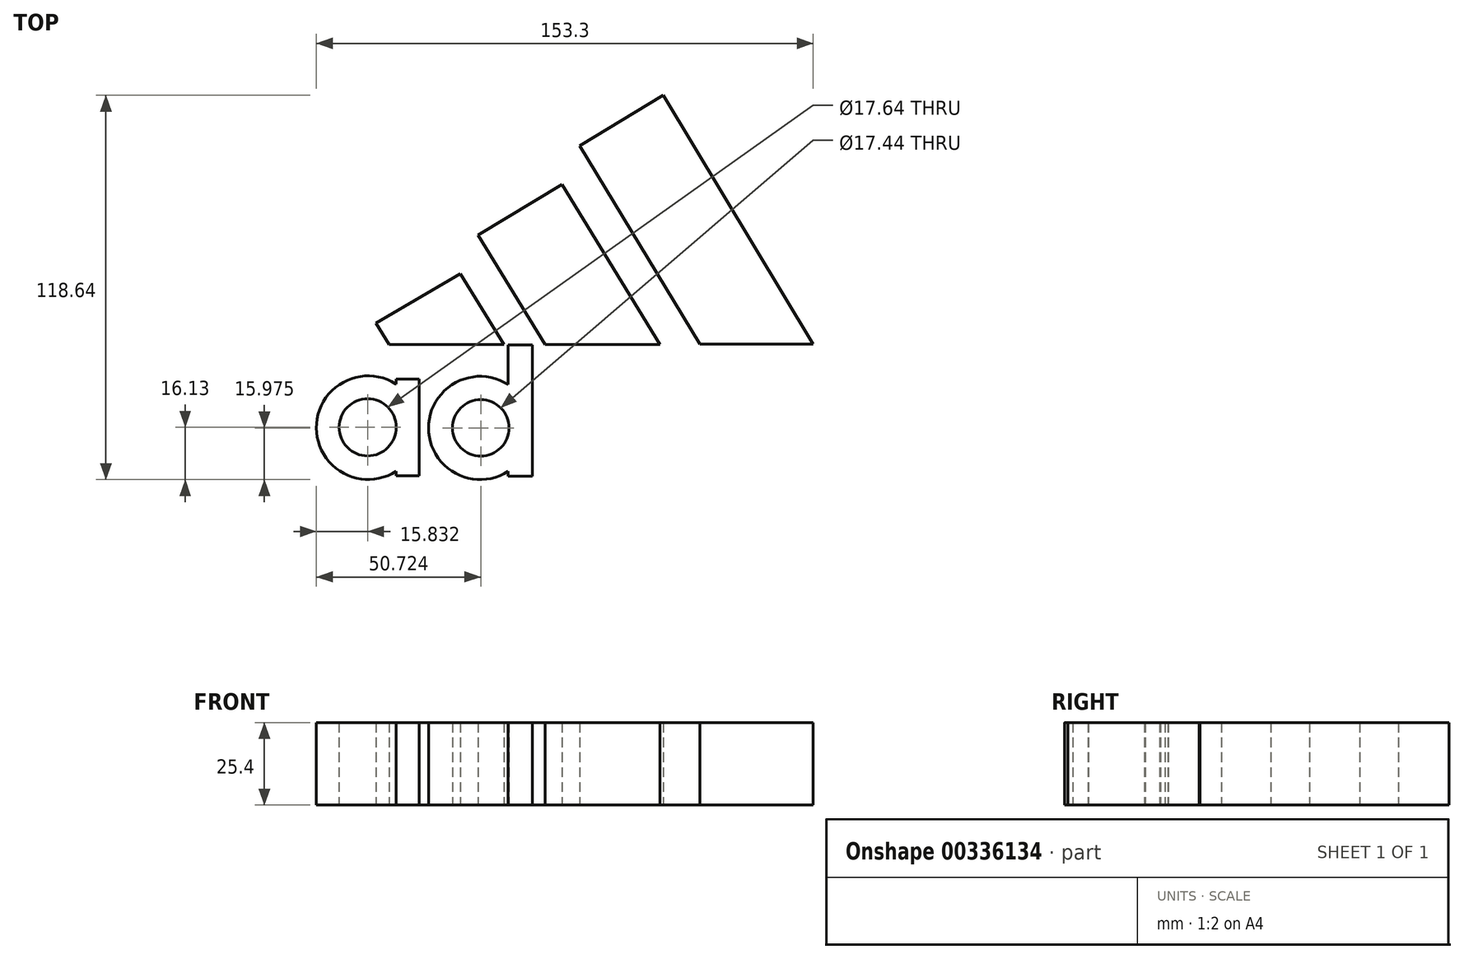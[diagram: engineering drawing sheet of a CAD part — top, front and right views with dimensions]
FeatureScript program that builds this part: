
annotation { "Feature Type Name" : "Feature", "Feature Type Description" : "" }
export const myFeature = defineFeature(function(context is Context, id is Id, definition is map)
    precondition{}
    {
        {
            var Q0;
            Q0=qCreatedBy(makeId("Top.planeOp"),FACE);
            var sketch = newSketch(context, id + "F0", { "sketchPlane" : qUnion([Q0])});
            skLineSegment(sketch, "E0", {"start": v(-45.16, 1.7) * mm, "end": v(-31.76, -20.22) * mm});
            skLineSegment(sketch, "E1", {"start": v(-31.76, -20.22) * mm, "end": v(-67.13, -20.22) * mm});
            skLineSegment(sketch, "E2", {"start": v(-67.13, -20.22) * mm, "end": v(-71.16, -13.54) * mm});
            skLineSegment(sketch, "E3", {"start": v(-71.16, -13.54) * mm, "end": v(-45.16, 1.7) * mm});
            skLineSegment(sketch, "E4", {"start": v(-13.78, 29.19) * mm, "end": v(16.4, -20.22) * mm});
            skLineSegment(sketch, "E5", {"start": v(16.4, -20.22) * mm, "end": v(-19, -20.22) * mm});
            skLineSegment(sketch, "E6", {"start": v(-19, -20.22) * mm, "end": v(-39.69, 13.63) * mm});
            skLineSegment(sketch, "E7", {"start": v(-39.69, 13.63) * mm, "end": v(-13.78, 29.19) * mm});
            skLineSegment(sketch, "E8", {"start": v(17.46, 56.75) * mm, "end": v(63.72, -20.11) * mm});
            skLineSegment(sketch, "E9", {"start": v(63.72, -20.11) * mm, "end": v(28.79, -20.11) * mm});
            skLineSegment(sketch, "E10", {"start": v(28.79, -20.11) * mm, "end": v(-8.37, 41.15) * mm});
            skLineSegment(sketch, "E11", {"start": v(-8.37, 41.15) * mm, "end": v(17.46, 56.75) * mm});
            skCircle(sketch, "E12", {"center": v(-73.75, -45.76) * mm, "radius": 8.82 * mm});
            skPoint(sketch, "E12.first.point", {"position": v(-73.75, -36.94) * mm});
            skPoint(sketch, "E12.second.point", {"position": v(-64.93, -45.5) * mm});
            skPoint(sketch, "E12.third.point", {"position": v(-80.69, -51.2) * mm});
            skArc(sketch, "E13", {"start": v(-65.08, -32.32) * mm, "mid": v(-89.58, -45.94) * mm, "end": v(-64.93, -59.3) * mm});
            skArc(sketch, "E14", {"start": v(-30.4, -32.55) * mm, "mid": v(-54.97, -45.93) * mm, "end": v(-30.43, -59.37) * mm});
            skCircle(sketch, "E15", {"center": v(-38.86, -45.92) * mm, "radius": 8.72 * mm});
            skPoint(sketch, "E15.first.point", {"position": v(-47.2, -48.44) * mm});
            skPoint(sketch, "E15.second.point", {"position": v(-30.62, -48.79) * mm});
            skPoint(sketch, "E15.third.point", {"position": v(-39.03, -37.2) * mm});
            skLineSegment(sketch, "E16", {"start": v(-64.93, -59.3) * mm, "end": v(-64.93, -60.76) * mm});
            skLineSegment(sketch, "E17", {"start": v(-64.93, -60.76) * mm, "end": v(-57.9, -60.76) * mm});
            skLineSegment(sketch, "E18", {"start": v(-57.9, -60.76) * mm, "end": v(-57.9, -30.85) * mm});
            skLineSegment(sketch, "E19", {"start": v(-57.9, -30.85) * mm, "end": v(-64.93, -30.85) * mm});
            skLineSegment(sketch, "E20", {"start": v(-64.93, -30.85) * mm, "end": v(-64.93, -32.32) * mm});
            skLineSegment(sketch, "E21", {"start": v(-64.93, -32.32) * mm, "end": v(-65.08, -32.32) * mm});
            skLineSegment(sketch, "E22", {"start": v(-30.43, -59.37) * mm, "end": v(-30.43, -60.87) * mm});
            skLineSegment(sketch, "E23", {"start": v(-30.43, -60.87) * mm, "end": v(-22.94, -60.87) * mm});
            skLineSegment(sketch, "E24", {"start": v(-22.94, -60.87) * mm, "end": v(-22.94, -20.37) * mm});
            skLineSegment(sketch, "E25", {"start": v(-22.94, -20.37) * mm, "end": v(-30.43, -20.37) * mm});
            skLineSegment(sketch, "E26", {"start": v(-30.43, -20.37) * mm, "end": v(-30.4, -32.55) * mm});
            skLineSegment(sketch, "E27", {"start": v(80.3, -39.34) * mm, "end": v(87.87, -39.34) * mm});
            skLineSegment(sketch, "E28", {"start": v(61.2, -50.88) * mm, "end": v(69.4, -50.88) * mm});
            skFitSpline(sketch, "E29", {"points": [v(69.4, -50.88) * mm, v(69.62, -52.9) * mm, v(71.9, -54.83) * mm, v(77.34, -55.27) * mm, v(79.83, -54.36) * mm, v(80.86, -53.3) * mm, v(80.66, -50.88) * mm], "startDerivative": vector(-0.72, -18.46) * mm, "endDerivative": vector(-8.64, 15.35) * mm});
            skSolve(sketch);
        }
        {
            var Q0;
            Q0=makeQuery(id+"F0.imprint","IMPRINT",FACE,{"disambiguationData":[TD([[makeQuery(id+"F0.imprint","IMPRINT",EDGE,{"derivedFrom":sQuery(id+"F0.wireOp",EDGE,"E8")}),-1.0]])]});
            var Q1;
            Q1=makeQuery(id+"F0.imprint","IMPRINT",FACE,{"disambiguationData":[TD([[makeQuery(id+"F0.imprint","IMPRINT",EDGE,{"derivedFrom":sQuery(id+"F0.wireOp",EDGE,"E0")}),-1.0]])]});
            var Q2;
            Q2=makeQuery(id+"F0.imprint","IMPRINT",FACE,{"disambiguationData":[TD([[makeQuery(id+"F0.imprint","IMPRINT",EDGE,{"derivedFrom":sQuery(id+"F0.wireOp",EDGE,"E4")}),-1.0]])]});
            var Q3;
            Q3=makeQuery(id+"F0.imprint","IMPRINT",FACE,{"disambiguationData":[TD([[makeQuery(id+"F0.imprint","IMPRINT",EDGE,{"derivedFrom":sQuery(id+"F0.wireOp",EDGE,"E12")}),-1.0]])]});
            var Q4;
            Q4=makeQuery(id+"F0.imprint","IMPRINT",FACE,{"disambiguationData":[TD([[makeQuery(id+"F0.imprint","IMPRINT",EDGE,{"derivedFrom":sQuery(id+"F0.wireOp",EDGE,"E14")}),1.0]])]});
            extrude(context, id + "F1", {"entities" : qUnion([Q0, Q1, Q2, Q3, Q4]), "depth" : 25.4 * mm});
        }
    });
